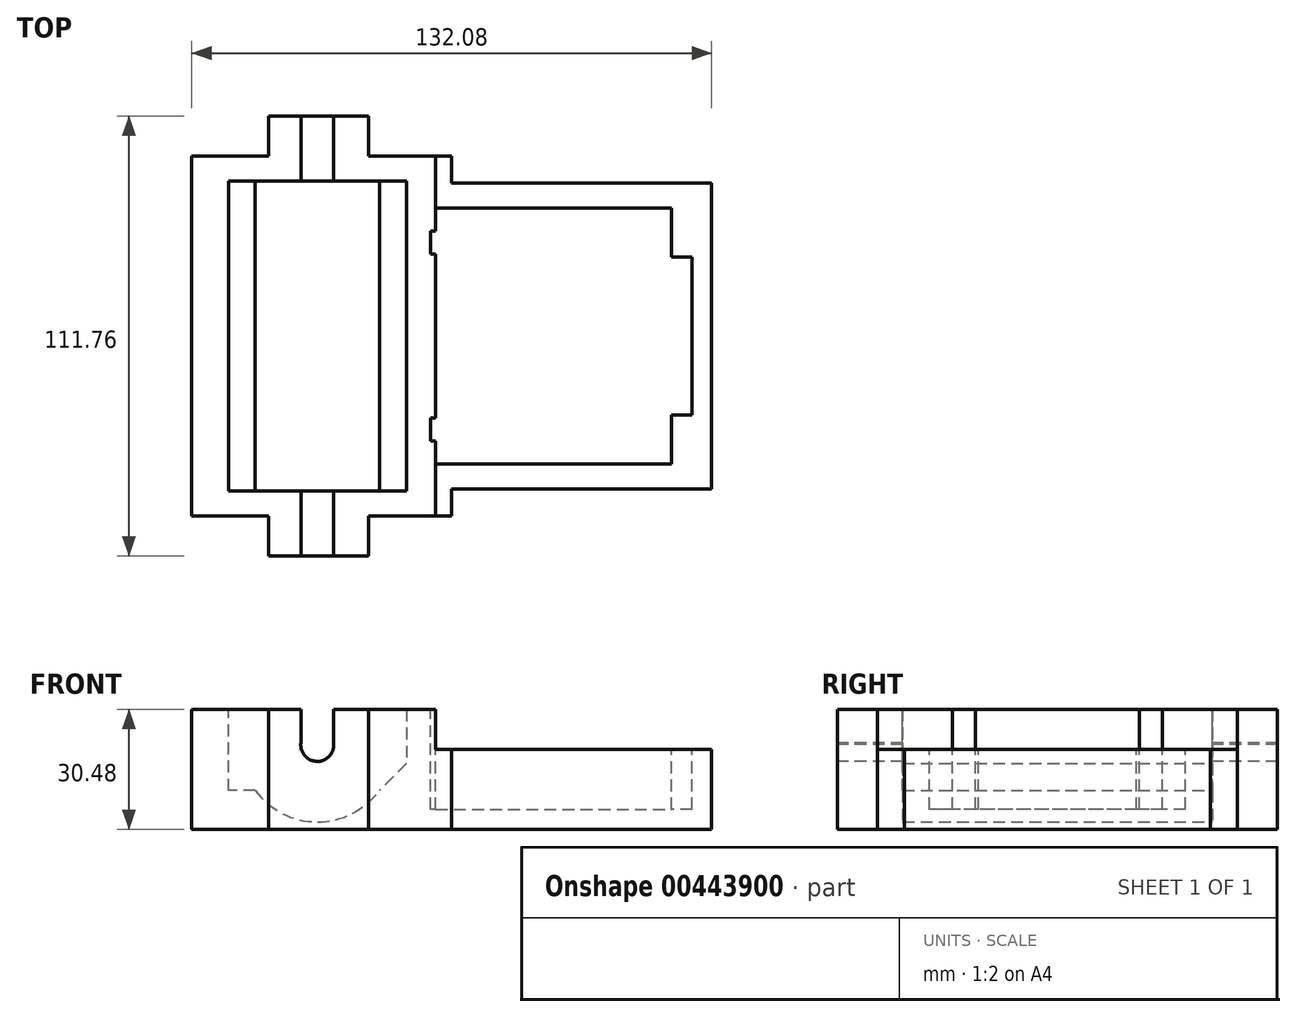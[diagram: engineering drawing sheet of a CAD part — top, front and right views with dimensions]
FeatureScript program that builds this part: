
annotation { "Feature Type Name" : "Feature", "Feature Type Description" : "" }
export const myFeature = defineFeature(function(context is Context, id is Id, definition is map)
    precondition{}
    {
        {
            var Q0;
            Q0=qCreatedBy(makeId("Top.planeOp"),FACE);
            var sketch = newSketch(context, id + "F0", { "sketchPlane" : qUnion([Q0])});
            skLineSegment(sketch, "E0.bottom", {"start": v(-66.04, 55.88) * mm, "end": v(66.04, 55.88) * mm});
            skLineSegment(sketch, "E0.top", {"start": v(-66.04, -55.88) * mm, "end": v(66.04, -55.88) * mm});
            skLineSegment(sketch, "E0.left", {"start": v(-66.04, 55.88) * mm, "end": v(-66.04, -55.88) * mm});
            skLineSegment(sketch, "E0.right", {"start": v(66.04, 55.88) * mm, "end": v(66.04, -55.88) * mm});
            skSolve(sketch);
        }
        {
            var Q0;
            Q0=qSketchRegion(id+"F0",true);
            extrude(context, id + "F1", {"entities" : qUnion([Q0]), "depth" : 30.48 * mm});
        }
        {
            var Q0;
            Q0=makeQuery(id+"F1.opExtrude","CAP_FACE",FACE,{"disambiguationData":[OSD([sQuery(id+"F0.wireOp",EDGE,"E0.bottom"),sQuery(id+"F0.wireOp",EDGE,"E0.top"),sQuery(id+"F0.wireOp",EDGE,"E0.left"),sQuery(id+"F0.wireOp",EDGE,"E0.right")])],"isStart":false});
            var sketch = newSketch(context, id + "F2", { "sketchPlane" : qUnion([Q0])});
            skLineSegment(sketch, "E1.bottom", {"start": v(-4.06, 32.51) * mm, "end": v(55.88, 32.51) * mm});
            skLineSegment(sketch, "E1.top", {"start": v(-4.06, -32.51) * mm, "end": v(55.88, -32.51) * mm});
            skLineSegment(sketch, "E1.left", {"start": v(-4.06, 32.51) * mm, "end": v(-4.06, 26.67) * mm});
            skLineSegment(sketch, "E1.right", {"start": v(55.88, 32.51) * mm, "end": v(55.88, 20.07) * mm});
            skLineSegment(sketch, "E2", {"start": v(55.88, 20.07) * mm, "end": v(61.05, 20.07) * mm});
            skLineSegment(sketch, "E3", {"start": v(61.05, 20.07) * mm, "end": v(61.05, -20.07) * mm});
            skLineSegment(sketch, "E4", {"start": v(61.05, -20.07) * mm, "end": v(55.88, -20.07) * mm});
            skLineSegment(sketch, "E5.trimOffspring", {"start": v(55.88, -20.07) * mm, "end": v(55.88, -32.51) * mm});
            skLineSegment(sketch, "E6", {"start": v(-4.06, 26.67) * mm, "end": v(-5.33, 26.67) * mm});
            skLineSegment(sketch, "E7", {"start": v(-5.33, 26.67) * mm, "end": v(-5.33, 20.83) * mm});
            skLineSegment(sketch, "E8", {"start": v(-5.33, 20.83) * mm, "end": v(-4.06, 20.83) * mm});
            skLineSegment(sketch, "E9", {"start": v(-4.06, -20.83) * mm, "end": v(-5.33, -20.83) * mm});
            skLineSegment(sketch, "E10", {"start": v(-5.33, -20.83) * mm, "end": v(-5.33, -26.67) * mm});
            skLineSegment(sketch, "E11", {"start": v(-5.33, -26.67) * mm, "end": v(-4.06, -26.67) * mm});
            skLineSegment(sketch, "E12.trimOffspring", {"start": v(-4.06, 20.83) * mm, "end": v(-4.06, -20.83) * mm});
            skLineSegment(sketch, "E13.trimOffspring", {"start": v(-4.06, -26.67) * mm, "end": v(-4.06, -32.51) * mm});
            skSolve(sketch);
        }
        {
            var Q0;
            Q0=qSketchRegion(id+"F2",true);
            extrude(context, id + "F3", {"entities" : qUnion([Q0]), "operationType" : NewBodyOperationType.REMOVE, "oppositeDirection" : true, "depth" : 25.4 * mm});
        }
        {
            var Q0;
            Q0=qCreatedBy(makeId("Front.planeOp"),FACE);
            var sketch = newSketch(context, id + "F4", { "sketchPlane" : qUnion([Q0])});
            skLineSegment(sketch, "E14", {"start": v(-34.16, 15.53) * mm, "end": v(-34.16, 21.48) * mm, "construction": true});
            skArc(sketch, "E15", {"start": v(-49.9, 9.88) * mm, "mid": v(-34.16, 1.92) * mm, "end": v(-18.41, 9.88) * mm});
            skLineSegment(sketch, "E16", {"start": v(-49.9, 9.88) * mm, "end": v(-18.41, 9.88) * mm, "construction": true});
            skLineSegment(sketch, "E17", {"start": v(-49.9, 9.88) * mm, "end": v(-56.77, 9.88) * mm});
            skLineSegment(sketch, "E18", {"start": v(-56.77, 9.88) * mm, "end": v(-56.77, 37.63) * mm});
            skLineSegment(sketch, "E19", {"start": v(-56.77, 37.63) * mm, "end": v(-11.55, 37.63) * mm});
            skLineSegment(sketch, "E20", {"start": v(-11.55, 37.63) * mm, "end": v(-11.55, 16.74) * mm});
            skLineSegment(sketch, "E21", {"start": v(-11.55, 16.74) * mm, "end": v(-18.41, 9.88) * mm});
            skLineSegment(sketch, "E22", {"start": v(-11.55, 16.74) * mm, "end": v(-11.55, 9.88) * mm, "construction": true});
            skLineSegment(sketch, "E23", {"start": v(-11.55, 9.88) * mm, "end": v(-18.41, 9.88) * mm, "construction": true});
            skSolve(sketch);
        }
        {
            var Q0;
            Q0=qSketchRegion(id+"F4",true);
            extrude(context, id + "F5", {"entities" : qUnion([Q0]), "operationType" : NewBodyOperationType.REMOVE, "depth" : 39.37 * mm, "hasSecondDirection" : true, "secondDirectionOppositeDirection" : true, "secondDirectionDepth" : 39.37 * mm});
        }
        {
            var Q0;
            Q0=qCreatedBy(makeId("Front.planeOp"),FACE);
            var sketch = newSketch(context, id + "F6", { "sketchPlane" : qUnion([Q0])});
            skArc(sketch, "E24", {"start": v(-38.33, 21.94) * mm, "mid": v(-34.35, 17.3) * mm, "end": v(-29.97, 21.57) * mm});
            skLineSegment(sketch, "E25", {"start": v(-29.97, 21.4) * mm, "end": v(-29.97, 31.2) * mm});
            skLineSegment(sketch, "E26", {"start": v(-38.33, 21.94) * mm, "end": v(-38.33, 31.2) * mm});
            skLineSegment(sketch, "E27", {"start": v(-38.33, 31.2) * mm, "end": v(-29.97, 31.2) * mm});
            skSolve(sketch);
        }
        {
            var Q0;
            Q0=qSketchRegion(id+"F6",true);
            extrude(context, id + "F7", {"entities" : qUnion([Q0]), "operationType" : NewBodyOperationType.REMOVE, "oppositeDirection" : true, "depth" : 127 * mm, "hasSecondDirection" : true, "secondDirectionOppositeDirection" : false, "secondDirectionDepth" : 127 * mm});
        }
        {
            var Q0;
            Q0=makeQuery(id+"F1.opExtrude","SWEPT_FACE",FACE,{"disambiguationData":[OSD([sQuery(id+"F0.wireOp",EDGE,"E0.top")])]});
            var sketch = newSketch(context, id + "F8", { "sketchPlane" : qUnion([Q0])});
            skLineSegment(sketch, "E28.bottom", {"start": v(-4.13, 30.48) * mm, "end": v(66.04, 30.48) * mm});
            skLineSegment(sketch, "E28.top", {"start": v(-4.13, 20.32) * mm, "end": v(66.04, 20.32) * mm});
            skLineSegment(sketch, "E28.left", {"start": v(-4.13, 30.48) * mm, "end": v(-4.13, 20.32) * mm});
            skLineSegment(sketch, "E28.right", {"start": v(66.04, 30.48) * mm, "end": v(66.04, 20.32) * mm});
            skSolve(sketch);
        }
        {
            var Q0;
            Q0=qSketchRegion(id+"F8",true);
            extrude(context, id + "F9", {"entities" : qUnion([Q0]), "operationType" : NewBodyOperationType.REMOVE, "oppositeDirection" : true, "depth" : 124.52 * mm});
        }
        {
            var Q0;
            {var subQ6=sQuery(id+"F0.wireOp",EDGE,"E0.left");var subQ7=sQuery(id+"F0.wireOp",EDGE,"E0.top");var subQ8=sQuery(id+"F0.wireOp",EDGE,"E0.bottom");Q0=makeQuery(id+"F7.boolean.opBoolean","SPLIT",FACE,{"disambiguationData":[TD([makeQuery(id+"F1.opExtrude","SWEPT_FACE",FACE,{"disambiguationData":[OSD([subQ6])]})])],"derivedFrom":makeQuery(id+"F1.opExtrude","CAP_FACE",FACE,{"disambiguationData":[OSD([subQ8,subQ7,subQ6,sQuery(id+"F0.wireOp",EDGE,"E0.right")])],"isStart":false})});}
            var sketch = newSketch(context, id + "F10", { "sketchPlane" : qUnion([Q0])});
            skLineSegment(sketch, "E29", {"start": v(-66.04, 45.72) * mm, "end": v(-46.48, 45.72) * mm});
            skLineSegment(sketch, "E30", {"start": v(-46.48, 45.72) * mm, "end": v(-46.48, 60.96) * mm});
            skLineSegment(sketch, "E31", {"start": v(-46.48, 60.96) * mm, "end": v(-21.08, 60.96) * mm});
            skLineSegment(sketch, "E32", {"start": v(-21.08, 60.96) * mm, "end": v(-21.08, 45.72) * mm});
            skLineSegment(sketch, "E33", {"start": v(-21.08, 45.72) * mm, "end": v(0, 45.72) * mm});
            skLineSegment(sketch, "E34", {"start": v(0, 45.72) * mm, "end": v(0, 38.86) * mm});
            skLineSegment(sketch, "E35", {"start": v(0, 38.86) * mm, "end": v(67.55, 38.86) * mm});
            skLineSegment(sketch, "E36", {"start": v(67.55, 38.86) * mm, "end": v(67.55, -38.86) * mm});
            skLineSegment(sketch, "E37", {"start": v(67.55, -38.86) * mm, "end": v(0, -38.86) * mm});
            skLineSegment(sketch, "E38", {"start": v(0, -38.86) * mm, "end": v(0, -45.72) * mm});
            skLineSegment(sketch, "E39", {"start": v(0, -45.72) * mm, "end": v(-21.08, -45.72) * mm});
            skLineSegment(sketch, "E40", {"start": v(-21.08, -45.72) * mm, "end": v(-21.08, -60.96) * mm});
            skLineSegment(sketch, "E41", {"start": v(-21.08, -60.96) * mm, "end": v(-46.48, -60.96) * mm});
            skLineSegment(sketch, "E42", {"start": v(-46.48, -60.96) * mm, "end": v(-46.48, -45.72) * mm});
            skLineSegment(sketch, "E43", {"start": v(-46.48, -45.72) * mm, "end": v(-66.04, -45.72) * mm});
            skLineSegment(sketch, "E44", {"start": v(-66.04, -45.72) * mm, "end": v(-66.04, 45.72) * mm});
            skLineSegment(sketch, "E45.bottom", {"start": v(-108.6, 91.7) * mm, "end": v(110.43, 91.7) * mm});
            skLineSegment(sketch, "E45.top", {"start": v(-108.6, -99.7) * mm, "end": v(110.43, -99.7) * mm});
            skLineSegment(sketch, "E45.left", {"start": v(-108.6, 91.7) * mm, "end": v(-108.6, -99.7) * mm});
            skLineSegment(sketch, "E45.right", {"start": v(110.43, 91.7) * mm, "end": v(110.43, -99.7) * mm});
            skSolve(sketch);
        }
        {
            var Q0;
            Q0=qSketchRegion(id+"F10",true);
            extrude(context, id + "F11", {"entities" : qUnion([Q0]), "operationType" : NewBodyOperationType.REMOVE, "oppositeDirection" : true, "depth" : 40.6 * mm});
        }
    });
